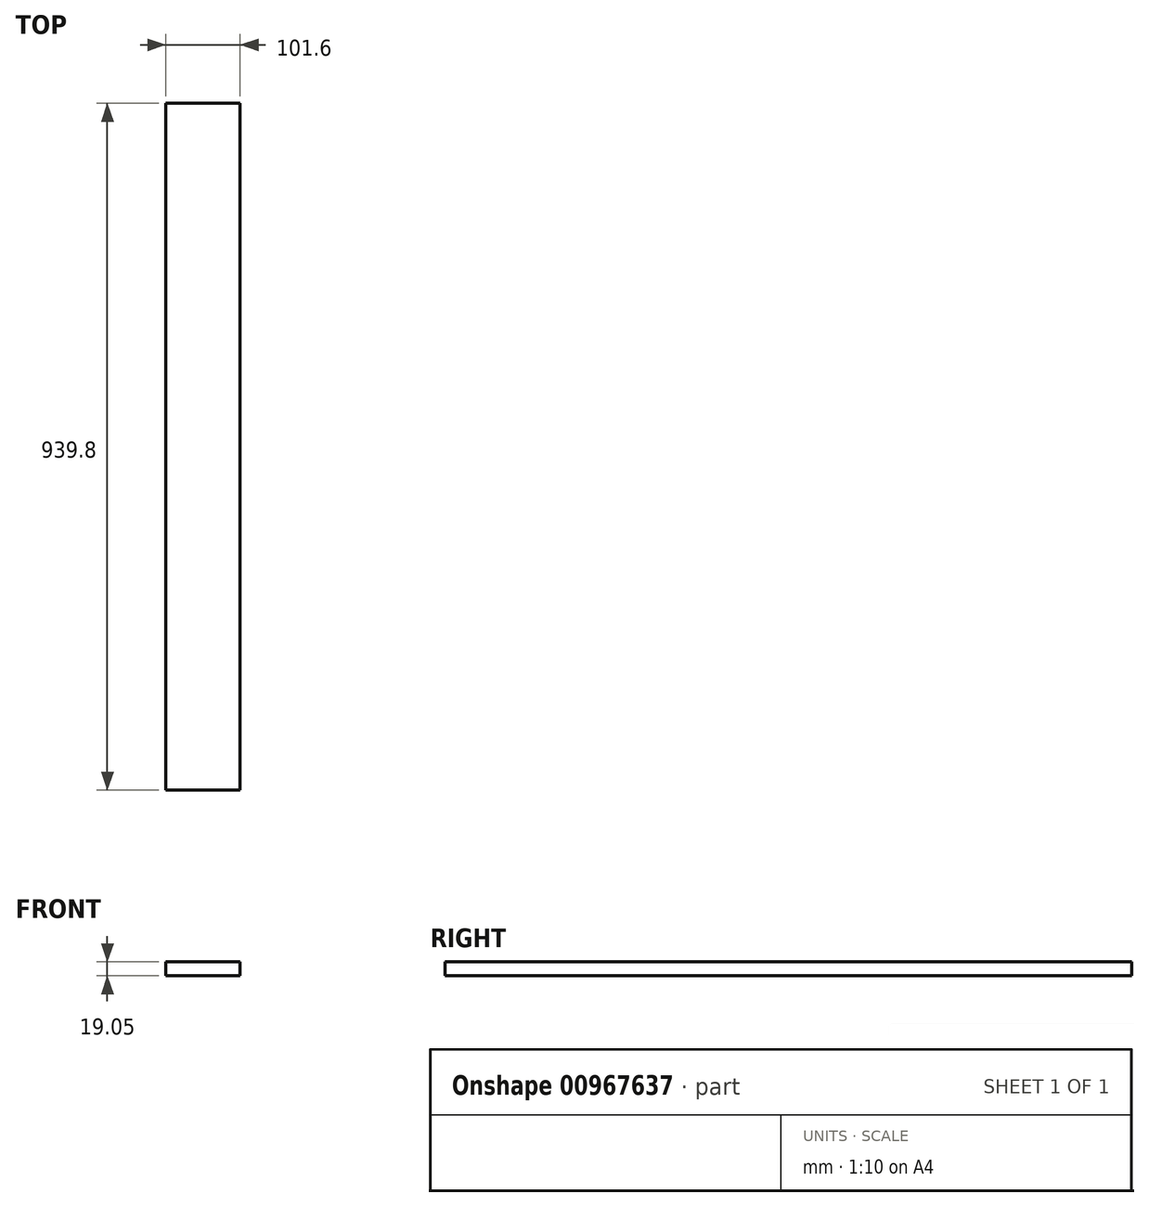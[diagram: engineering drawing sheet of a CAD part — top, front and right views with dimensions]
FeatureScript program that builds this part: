
annotation { "Feature Type Name" : "Feature", "Feature Type Description" : "" }
export const myFeature = defineFeature(function(context is Context, id is Id, definition is map)
    precondition{}
    {
        {
            var Q0;
            Q0=qCreatedBy(makeId("Top.planeOp"),FACE);
            var sketch = newSketch(context, id + "F0", { "sketchPlane" : qUnion([Q0])});
            skLineSegment(sketch, "E0.bottom", {"start": v(0, 0) * mm, "end": v(101.6, 0) * mm});
            skLineSegment(sketch, "E0.top", {"start": v(0, 939.8) * mm, "end": v(101.6, 939.8) * mm});
            skLineSegment(sketch, "E0.left", {"start": v(0, 0) * mm, "end": v(0, 939.8) * mm});
            skLineSegment(sketch, "E0.right", {"start": v(101.6, 0) * mm, "end": v(101.6, 939.8) * mm});
            skSolve(sketch);
        }
        {
            var Q0;
            Q0 = qSketchRegion(id + "F0", true);
            extrude(context, id + "F1", {"entities" : qUnion([Q0]), "depth" : 19.05 * mm, "offsetDistance" : 25.4 * mm});
        }
    });
